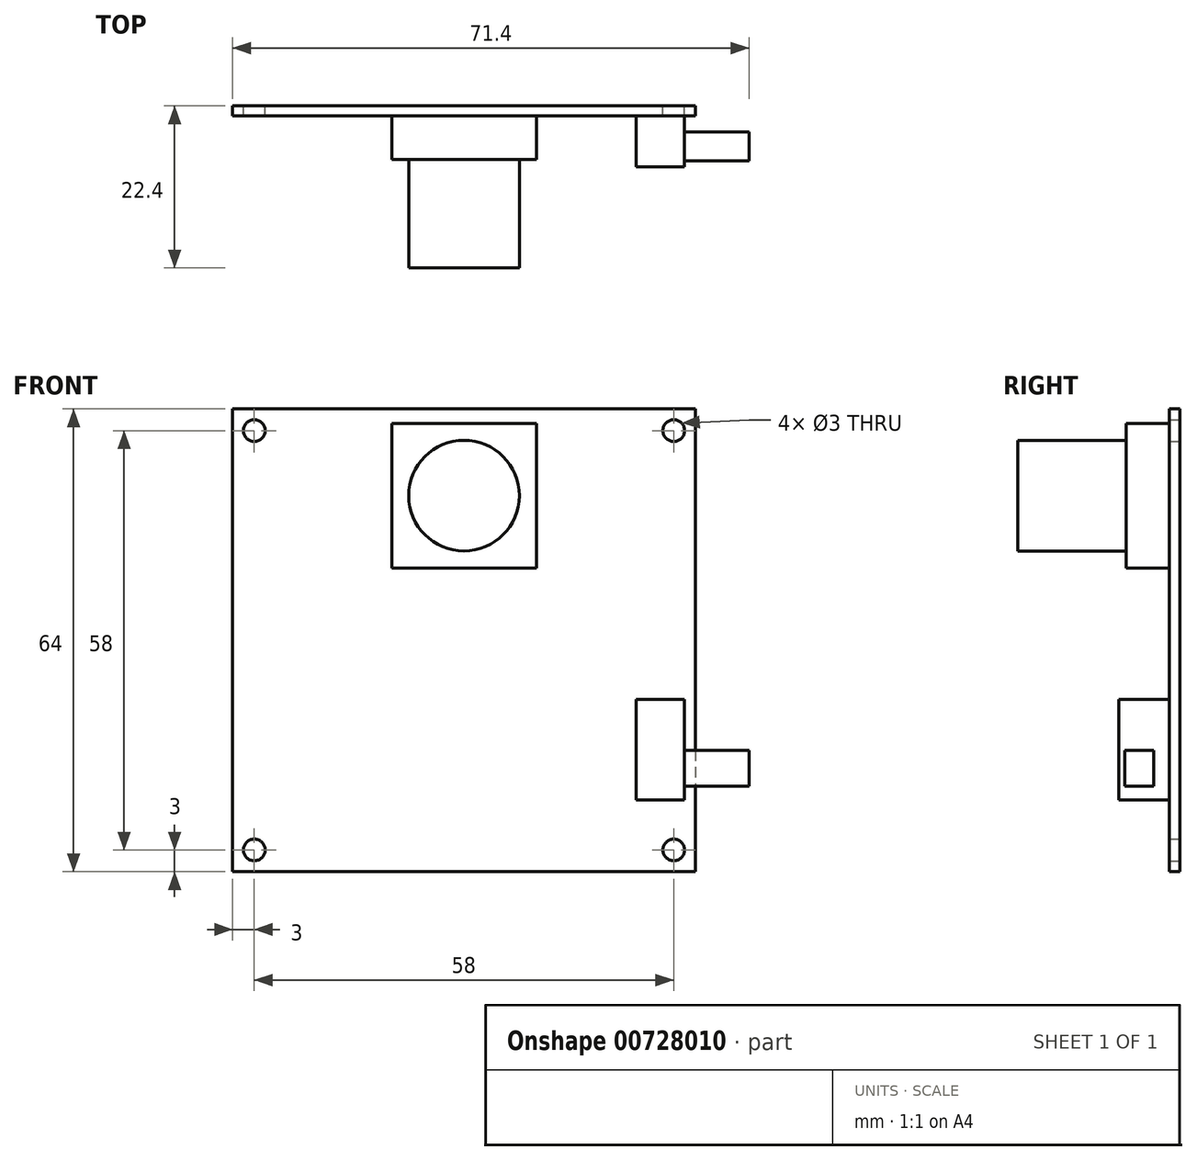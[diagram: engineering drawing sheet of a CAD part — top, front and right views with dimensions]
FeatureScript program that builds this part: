
annotation { "Feature Type Name" : "Feature", "Feature Type Description" : "" }
export const myFeature = defineFeature(function(context is Context, id is Id, definition is map)
    precondition{}
    {
        {
            var Q0;
            Q0=qCreatedBy(makeId("Front.planeOp"),FACE);
            var sketch = newSketch(context, id + "F0", { "sketchPlane" : qUnion([Q0])});
            skLineSegment(sketch, "E0.bottom", {"start": v(32, 32) * mm, "end": v(-32, 32) * mm});
            skLineSegment(sketch, "E0.top", {"start": v(32, -32) * mm, "end": v(-32, -32) * mm});
            skLineSegment(sketch, "E0.left", {"start": v(32, 32) * mm, "end": v(32, -32) * mm});
            skLineSegment(sketch, "E0.right", {"start": v(-32, 32) * mm, "end": v(-32, -32) * mm});
            skPoint(sketch, "E0.middle", {"position": v(0, 0) * mm});
            skCircle(sketch, "E1", {"center": v(-29, 29) * mm, "radius": 1.5 * mm});
            skCircle(sketch, "E2.MirrorC", {"center": v(29, 29) * mm, "radius": 1.5 * mm});
            skCircle(sketch, "E3.MirrorC", {"center": v(-29, -29) * mm, "radius": 1.5 * mm});
            skCircle(sketch, "E4.MirrorC", {"center": v(29, -29) * mm, "radius": 1.5 * mm});
            skSolve(sketch);
        }
        {
            var Q0;
            Q0=makeQuery(id+"F0.imprint","IMPRINT",FACE,{"disambiguationData":[TD([[makeQuery(id+"F0.imprint","IMPRINT",EDGE,{"derivedFrom":sQuery(id+"F0.wireOp",EDGE,"E0.bottom")}),1.0]])]});
            extrude(context, id + "F1", {"entities" : qUnion([Q0]), "depth" : 1.4 * mm, "offsetDistance" : 25 * mm});
        }
        {
            var Q0;
            Q0=makeQuery(id+"F1.opExtrude","CAP_FACE",FACE,{"disambiguationData":[OSD([sQuery(id+"F0.wireOp",EDGE,"E0.bottom"),sQuery(id+"F0.wireOp",EDGE,"E0.top"),sQuery(id+"F0.wireOp",EDGE,"E0.left"),sQuery(id+"F0.wireOp",EDGE,"E0.right"),sQuery(id+"F0.wireOp",EDGE,"E1"),sQuery(id+"F0.wireOp",EDGE,"E2.MirrorC"),sQuery(id+"F0.wireOp",EDGE,"E3.MirrorC"),sQuery(id+"F0.wireOp",EDGE,"E4.MirrorC")])],"isStart":false});
            var sketch = newSketch(context, id + "F2", { "sketchPlane" : qUnion([Q0])});
            skLineSegment(sketch, "E5.bottom", {"start": v(10, 30) * mm, "end": v(-10, 30) * mm});
            skLineSegment(sketch, "E5.top", {"start": v(10, 10) * mm, "end": v(-10, 10) * mm});
            skLineSegment(sketch, "E5.left", {"start": v(10, 30) * mm, "end": v(10, 10) * mm});
            skLineSegment(sketch, "E5.right", {"start": v(-10, 30) * mm, "end": v(-10, 10) * mm});
            skCircle(sketch, "E6", {"center": v(0, 20) * mm, "radius": 7.65 * mm});
            skPoint(sketch, "E6.centerSnap0", {"position": v(-10, 20) * mm});
            skLineSegment(sketch, "E7.bottom", {"start": v(30.5, -8.2) * mm, "end": v(23.8, -8.2) * mm});
            skLineSegment(sketch, "E7.top", {"start": v(30.5, -22.1) * mm, "end": v(23.8, -22.1) * mm});
            skLineSegment(sketch, "E7.left", {"start": v(30.5, -8.2) * mm, "end": v(30.5, -22.1) * mm});
            skLineSegment(sketch, "E7.right", {"start": v(23.8, -8.2) * mm, "end": v(23.8, -22.1) * mm});
            skSolve(sketch);
        }
        {
            var Q0;
            Q0=makeQuery(id+"F2.imprint","IMPRINT",FACE,{"disambiguationData":[TD([[makeQuery(id+"F2.imprint","IMPRINT",EDGE,{"derivedFrom":sQuery(id+"F2.wireOp",EDGE,"E5.bottom")}),1.0]])]});
            extrude(context, id + "F3", {"entities" : qUnion([Q0]), "operationType" : NewBodyOperationType.ADD, "depth" : 6 * mm, "offsetDistance" : 25 * mm});
        }
        {
            var Q0;
            Q0=makeQuery(id+"F3.boolean.opBoolean","SPLIT",FACE,{"disambiguationData":[TD([makeQuery(id+"F3.opExtrude","SWEPT_FACE",FACE,{"disambiguationData":[OSD([sQuery(id+"F2.wireOp",EDGE,"E6")])]})])],"derivedFrom":makeQuery(id+"F1.opExtrude","CAP_FACE",FACE,{"disambiguationData":[OSD([sQuery(id+"F0.wireOp",EDGE,"E0.bottom"),sQuery(id+"F0.wireOp",EDGE,"E0.top"),sQuery(id+"F0.wireOp",EDGE,"E0.left"),sQuery(id+"F0.wireOp",EDGE,"E0.right"),sQuery(id+"F0.wireOp",EDGE,"E1"),sQuery(id+"F0.wireOp",EDGE,"E2.MirrorC"),sQuery(id+"F0.wireOp",EDGE,"E3.MirrorC"),sQuery(id+"F0.wireOp",EDGE,"E4.MirrorC")])],"isStart":false})});
            extrude(context, id + "F4", {"entities" : qUnion([Q0]), "operationType" : NewBodyOperationType.ADD, "depth" : 21 * mm, "offsetDistance" : 25 * mm});
        }
        {
            var Q0;
            Q0=makeQuery(id+"F2.imprint","IMPRINT",FACE,{"disambiguationData":[TD([[makeQuery(id+"F2.imprint","IMPRINT",EDGE,{"derivedFrom":sQuery(id+"F2.wireOp",EDGE,"E7.bottom")}),1.0]])]});
            extrude(context, id + "F5", {"entities" : qUnion([Q0]), "operationType" : NewBodyOperationType.ADD, "depth" : 7 * mm, "offsetDistance" : 25 * mm});
        }
        {
            var Q0;
            Q0=makeQuery(id+"F5.opExtrude","SWEPT_FACE",FACE,{"disambiguationData":[OSD([sQuery(id+"F2.wireOp",EDGE,"E7.left")])]});
            var sketch = newSketch(context, id + "F6", { "sketchPlane" : qUnion([Q0])});
            skLineSegment(sketch, "E8.bottom", {"start": v(-7.6, -20.2) * mm, "end": v(-3.6, -20.2) * mm});
            skLineSegment(sketch, "E8.top", {"start": v(-7.6, -15.2) * mm, "end": v(-3.6, -15.2) * mm});
            skLineSegment(sketch, "E8.left", {"start": v(-7.6, -20.2) * mm, "end": v(-7.6, -15.2) * mm});
            skLineSegment(sketch, "E8.right", {"start": v(-3.6, -20.2) * mm, "end": v(-3.6, -15.2) * mm});
            skSolve(sketch);
        }
        {
            var Q0;
            Q0=makeQuery(id+"F6.imprint","IMPRINT",FACE,{"disambiguationData":[TD([[makeQuery(id+"F6.imprint","IMPRINT",EDGE,{"derivedFrom":sQuery(id+"F6.wireOp",EDGE,"E8.bottom")}),1.0]])]});
            extrude(context, id + "F7", {"entities" : qUnion([Q0]), "operationType" : NewBodyOperationType.ADD, "depth" : 8.9 * mm, "offsetDistance" : 25 * mm});
        }
    });
